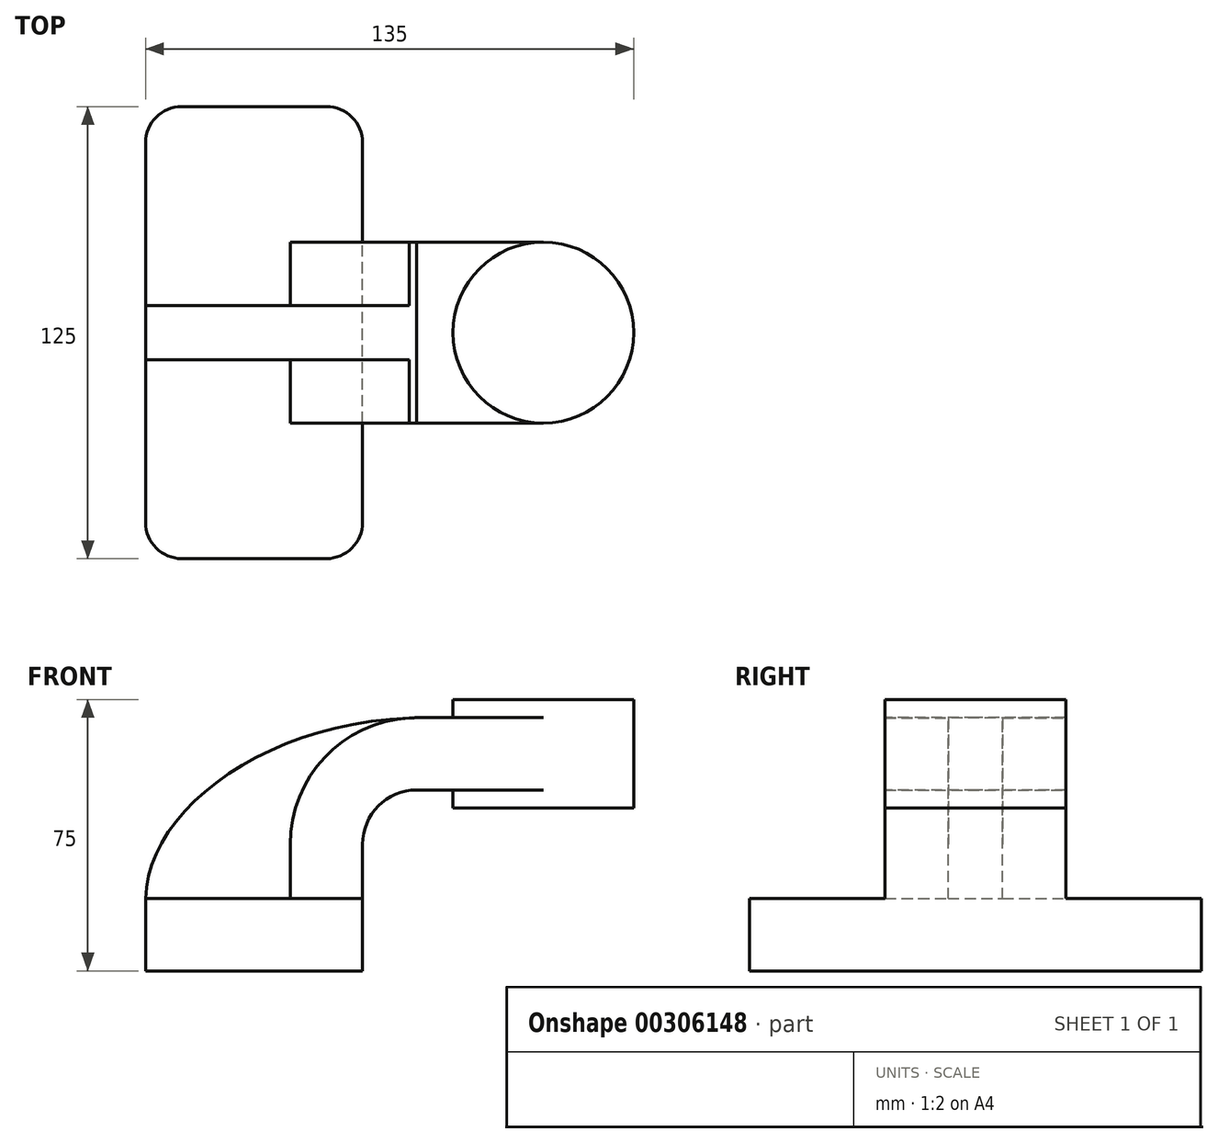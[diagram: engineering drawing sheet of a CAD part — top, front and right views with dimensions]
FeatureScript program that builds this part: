
annotation { "Feature Type Name" : "Feature", "Feature Type Description" : "" }
export const myFeature = defineFeature(function(context is Context, id is Id, definition is map)
    precondition{}
    {
        {
            var Q0;
            Q0=qCreatedBy(makeId("Front.planeOp"),FACE);
            var sketch = newSketch(context, id + "F0", { "sketchPlane" : qUnion([Q0])});
            skLineSegment(sketch, "E0.bottom", {"start": v(-30, 10) * mm, "end": v(30, 10) * mm});
            skLineSegment(sketch, "E0.top", {"start": v(-30, -10) * mm, "end": v(30, -10) * mm});
            skLineSegment(sketch, "E0.left", {"start": v(-30, 10) * mm, "end": v(-30, -10) * mm});
            skLineSegment(sketch, "E0.right", {"start": v(30, 10) * mm, "end": v(30, -10) * mm});
            skPoint(sketch, "E0.middle", {"position": v(0, 0) * mm});
            skLineSegment(sketch, "E1.bottom", {"start": v(105, 65) * mm, "end": v(55, 65) * mm});
            skLineSegment(sketch, "E1.top", {"start": v(105, 35) * mm, "end": v(55, 35) * mm});
            skLineSegment(sketch, "E1.left", {"start": v(105, 65) * mm, "end": v(105, 35) * mm});
            skLineSegment(sketch, "E1.right", {"start": v(55, 65) * mm, "end": v(55, 35) * mm});
            skPoint(sketch, "E1.middle", {"position": v(80, 50) * mm});
            skLineSegment(sketch, "E2", {"start": v(30, 10) * mm, "end": v(30, 25) * mm});
            skArc(sketch, "E3", {"start": v(30, 25) * mm, "mid": v(34.4, 35.6) * mm, "end": v(45, 40) * mm});
            skLineSegment(sketch, "E4", {"start": v(45, 40) * mm, "end": v(80, 40) * mm});
            skLineSegment(sketch, "E5.0", {"start": v(45, 60) * mm, "end": v(80, 60) * mm});
            skArc(sketch, "E5.1", {"start": v(10, 25) * mm, "mid": v(20.25, 49.75) * mm, "end": v(45, 60) * mm});
            skLineSegment(sketch, "E5.2", {"start": v(10, 10) * mm, "end": v(10, 25) * mm});
            skFitSpline(sketch, "E6", {"points": [v(-30, 10) * mm, v(45, 60) * mm], "startDerivative": vector(1.25, 72.7) * mm, "endDerivative": vector(125.74, 2.5) * mm});
            skLineSegment(sketch, "E7", {"start": v(80, 40) * mm, "end": v(80, 60) * mm});
            skLineSegment(sketch, "E8", {"start": v(80, 60) * mm, "end": v(80, 65) * mm});
            skLineSegment(sketch, "E9", {"start": v(80, 40) * mm, "end": v(80, 35) * mm});
            skSolve(sketch);
        }
        {
            var Q0;
            Q0=makeQuery(id+"F0.imprint","IMPRINT",FACE,{"disambiguationData":[TD([[makeQuery(id+"F0.imprint","IMPRINT",EDGE,{"derivedFrom":sQuery(id+"F0.wireOp",EDGE,"E0.top")}),1.0]])]});
            extrude(context, id + "F1", {"entities" : qUnion([Q0]), "endBound" : BoundingType.SYMMETRIC, "depth" : 125 * mm});
        }
        {
            var Q0;
            {var subQ1=sQuery(id+"F0.wireOp",EDGE,"E2");Q0=makeQuery(id+"F0.imprint","IMPRINT",FACE,{"disambiguationData":[TD([[makeQuery(id+"F0.imprint","IMPRINT",EDGE,{"derivedFrom":subQ1}),1.0]])]});}
            var Q1;
            {var subQ5=sQuery(id+"F0.wireOp",EDGE,"E7");Q1=makeQuery(id+"F0.imprint","IMPRINT",FACE,{"disambiguationData":[TD([[makeQuery(id+"F0.imprint","IMPRINT",EDGE,{"derivedFrom":subQ5}),1.0]])]});}
            extrude(context, id + "F2", {"entities" : qUnion([Q0, Q1]), "operationType" : NewBodyOperationType.ADD, "endBound" : BoundingType.SYMMETRIC, "depth" : 50 * mm});
        }
        {
            var Q0;
            {var subQ3=sQuery(id+"F0.wireOp",EDGE,"E5.2");Q0=makeQuery(id+"F0.imprint","IMPRINT",FACE,{"disambiguationData":[TD([[makeQuery(id+"F0.imprint","IMPRINT",EDGE,{"derivedFrom":subQ3}),1.0]])]});}
            extrude(context, id + "F3", {"entities" : qUnion([Q0]), "operationType" : NewBodyOperationType.ADD, "endBound" : BoundingType.SYMMETRIC, "depth" : 15 * mm});
        }
        {
            var Q0;
            {var subQ0=sQuery(id+"F0.wireOp",EDGE,"E1.left");Q0=makeQuery(id+"F0.imprint","IMPRINT",FACE,{"disambiguationData":[TD([[makeQuery(id+"F0.imprint","IMPRINT",EDGE,{"derivedFrom":subQ0}),-1.0]])]});}
            var Q1;
            Q1=sQuery(id+"F0.wireOp",EDGE,"E7");
            revolve(context, id + "F4", {"operationType" : NewBodyOperationType.ADD, "entities" : qUnion([Q0]), "axis" : qUnion([Q1]), "revolveType" : RevolveType.FULL});
        }
        {
            var Q0;
            Q0=makeQuery(id+"F1.opExtrude","CAP_EDGE",EDGE,{"disambiguationData":[OSD([sQuery(id+"F0.wireOp",EDGE,"E0.left")])],"isStart":false});
            var Q1;
            Q1=makeQuery(id+"F1.opExtrude","CAP_EDGE",EDGE,{"disambiguationData":[OSD([sQuery(id+"F0.wireOp",EDGE,"E0.right")])],"isStart":false});
            var Q2;
            Q2=makeQuery(id+"F1.opExtrude","CAP_EDGE",EDGE,{"disambiguationData":[OSD([sQuery(id+"F0.wireOp",EDGE,"E0.right")])],"isStart":true});
            var Q3;
            Q3=makeQuery(id+"F1.opExtrude","CAP_EDGE",EDGE,{"disambiguationData":[OSD([sQuery(id+"F0.wireOp",EDGE,"E0.left")])],"isStart":true});
            fillet(context, id + "F5", {"entities" : qUnion([Q0, Q1, Q2, Q3]), "radius" : 10 * mm, "tangentPropagation" : true, "allowEdgeOverflow" : false});
        }
    });
